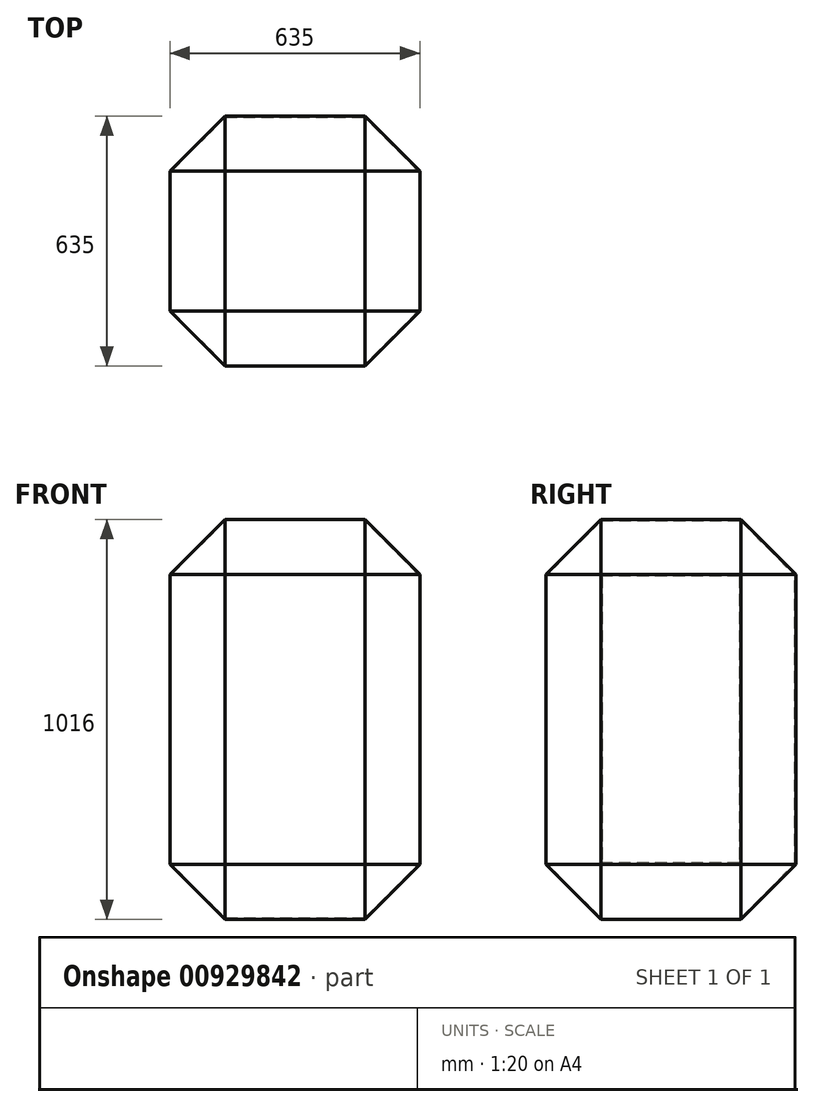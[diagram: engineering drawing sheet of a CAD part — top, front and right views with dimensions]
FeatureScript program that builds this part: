
annotation { "Feature Type Name" : "Feature", "Feature Type Description" : "" }
export const myFeature = defineFeature(function(context is Context, id is Id, definition is map)
    precondition{}
    {
        {
            var Q0;
            Q0=qCreatedBy(makeId("Front.planeOp"),FACE);
            var sketch = newSketch(context, id + "F0", { "sketchPlane" : qUnion([Q0])});
            skLineSegment(sketch, "E0.bottom", {"start": v(-319.68, -425.3) * mm, "end": v(315.32, -425.3) * mm});
            skLineSegment(sketch, "E0.top", {"start": v(-319.68, 590.7) * mm, "end": v(315.32, 590.7) * mm});
            skLineSegment(sketch, "E0.left", {"start": v(-319.68, -425.3) * mm, "end": v(-319.68, 590.7) * mm});
            skLineSegment(sketch, "E0.right", {"start": v(315.32, -425.3) * mm, "end": v(315.32, 590.7) * mm});
            skSolve(sketch);
        }
        {
            var Q0;
            Q0=makeQuery(id+"F0.imprint","IMPRINT",FACE,{"disambiguationData":[TD([[makeQuery(id+"F0.imprint","IMPRINT",EDGE,{"derivedFrom":sQuery(id+"F0.wireOp",EDGE,"E0.bottom")}),1.0]])]});
            extrude(context, id + "F1", {"entities" : qUnion([Q0]), "depth" : 635 * mm, "offsetDistance" : 25.4 * mm});
        }
        {
            var Q0;
            Q0=makeQuery(id+"F1.opExtrude","SWEPT_EDGE",EDGE,{"disambiguationData":[OSD([sQuery(id+"F0.wireOp",EDGE,"E0.top"),sQuery(id+"F0.wireOp",EDGE,"E0.right")])]});
            var Q1;
            Q1=makeQuery(id+"F1.opExtrude","CAP_EDGE",EDGE,{"disambiguationData":[OSD([sQuery(id+"F0.wireOp",EDGE,"E0.top")])],"isStart":false});
            var Q2;
            Q2=makeQuery(id+"F1.opExtrude","SWEPT_EDGE",EDGE,{"disambiguationData":[OSD([sQuery(id+"F0.wireOp",EDGE,"E0.top"),sQuery(id+"F0.wireOp",EDGE,"E0.left")])]});
            var Q3;
            Q3=makeQuery(id+"F1.opExtrude","CAP_EDGE",EDGE,{"disambiguationData":[OSD([sQuery(id+"F0.wireOp",EDGE,"E0.top")])],"isStart":true});
            var Q4;
            Q4=makeQuery(id+"F1.opExtrude","CAP_EDGE",EDGE,{"disambiguationData":[OSD([sQuery(id+"F0.wireOp",EDGE,"E0.right")])],"isStart":false});
            var Q5;
            Q5=makeQuery(id+"F1.opExtrude","CAP_EDGE",EDGE,{"disambiguationData":[OSD([sQuery(id+"F0.wireOp",EDGE,"E0.right")])],"isStart":true});
            var Q6;
            Q6=makeQuery(id+"F1.opExtrude","CAP_EDGE",EDGE,{"disambiguationData":[OSD([sQuery(id+"F0.wireOp",EDGE,"E0.left")])],"isStart":false});
            var Q7;
            Q7=makeQuery(id+"F1.opExtrude","CAP_EDGE",EDGE,{"disambiguationData":[OSD([sQuery(id+"F0.wireOp",EDGE,"E0.bottom")])],"isStart":false});
            var Q8;
            Q8=makeQuery(id+"F1.opExtrude","SWEPT_EDGE",EDGE,{"disambiguationData":[OSD([sQuery(id+"F0.wireOp",EDGE,"E0.bottom"),sQuery(id+"F0.wireOp",EDGE,"E0.right")])]});
            var Q9;
            Q9=makeQuery(id+"F1.opExtrude","CAP_EDGE",EDGE,{"disambiguationData":[OSD([sQuery(id+"F0.wireOp",EDGE,"E0.left")])],"isStart":true});
            var Q10;
            Q10=makeQuery(id+"F1.opExtrude","SWEPT_EDGE",EDGE,{"disambiguationData":[OSD([sQuery(id+"F0.wireOp",EDGE,"E0.bottom"),sQuery(id+"F0.wireOp",EDGE,"E0.left")])]});
            var Q11;
            Q11=makeQuery(id+"F1.opExtrude","CAP_EDGE",EDGE,{"disambiguationData":[OSD([sQuery(id+"F0.wireOp",EDGE,"E0.bottom")])],"isStart":true});
            chamfer(context, id + "F2", {"entities" : qUnion([Q0, Q1, Q2, Q3, Q4, Q5, Q6, Q7, Q8, Q9, Q10, Q11]), "width" : 139.7 * mm, "tangentPropagation" : true});
        }
        {
            var Q0;
            Q0=makeQuery(id+"F1.opExtrude","SWEPT_FACE",FACE,{"disambiguationData":[OSD([sQuery(id+"F0.wireOp",EDGE,"E0.left")])]});
            shell(context, id + "F3", {"entities" : qUnion([Q0]), "thickness" : 2.54 * mm});
        }
    });
